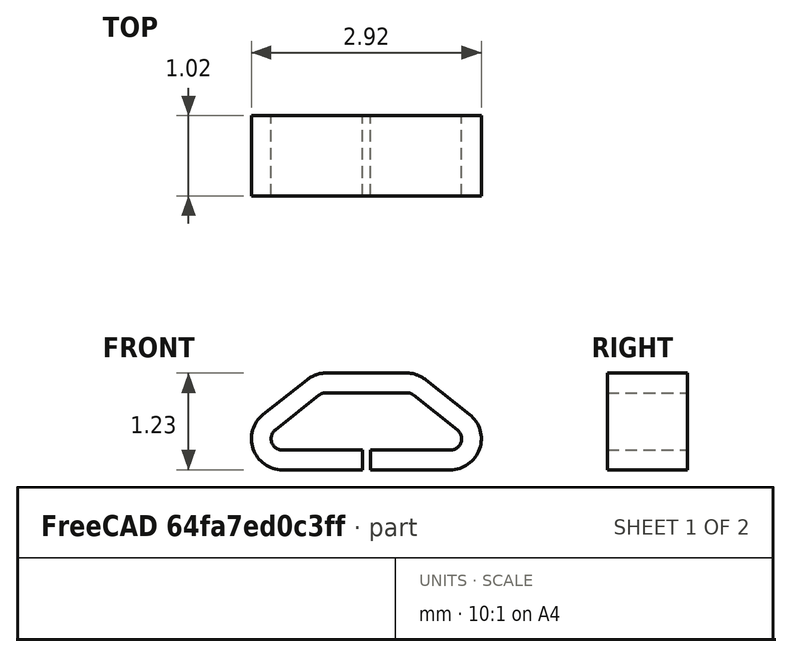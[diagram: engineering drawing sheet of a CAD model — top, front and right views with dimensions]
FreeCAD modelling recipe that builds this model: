
FCSTD DOCUMENT  (FreeCAD 1.0R39109 (Git))
Label: RH-5015
License: All rights reserved
LicenseURL: http://en.wikipedia.org/wiki/All_rights_reserved
objects: Sketcher::SketchObject×2, PartDesign::AdditivePipe×1, PartDesign::Body×1
note: 8 computed .brp shape members not serialized (recipe doc carries the construction recipe); baked Part::Feature solids carry a one-line shape summary decoded from their .brp

FEATURE [Sketcher::SketchObject] Sketch  label="RH-5015 trj"
  ArcFitTolerance = 1e-06
  AttachmentSupport = -> [XZ_Plane]
  FullyConstrained = true
  MakeInternals = false
  MapMode = 5
  Placement = pos=(0,0,0) rot=(1,0,0;1.5708rad)
  sketch-geometry (13):
    g0: LineSegment StartX=0.05 StartY=0.125 StartZ=0 EndX=1.065 EndY=0.125 EndZ=0
    g1: LineSegment StartX=1.23274 StartY=0.606576 StartZ=0 EndX=0.677736 EndY=1.04658 EndZ=0
    g2: LineSegment StartX=0.51 StartY=1.105 StartZ=0 EndX=-0.51 EndY=1.105 EndZ=0
    g3: LineSegment StartX=-0.677736 StartY=1.04658 StartZ=0 EndX=-1.23274 EndY=0.606576 EndZ=0
    g4: LineSegment StartX=-1.065 StartY=0.125 StartZ=0 EndX=-0.05 EndY=0.125 EndZ=0
    g5: ArcOfCircle CenterX=1.065 CenterY=0.395 CenterZ=0 NormalX=0 NormalY=0 NormalZ=1 AngleXU=0 Radius=0.27 StartAngle=4.71239 EndAngle=7.18365
    g6: GeomPoint [constr] X=1.84018 Y=0.125 Z=0
    g7: ArcOfCircle CenterX=0.51 CenterY=0.835 CenterZ=0 NormalX=0 NormalY=0 NormalZ=1 AngleXU=0 Radius=0.27 StartAngle=0.900465 EndAngle=1.5708
    g8: GeomPoint [constr] X=0.604043 Y=1.105 Z=0
    g9: ArcOfCircle CenterX=-0.51 CenterY=0.835 CenterZ=0 NormalX=0 NormalY=0 NormalZ=1 AngleXU=0 Radius=0.27 StartAngle=1.5708 EndAngle=2.24113
    g10: GeomPoint [constr] X=-0.604043 Y=1.105 Z=0
    g11: ArcOfCircle CenterX=-1.065 CenterY=0.395 CenterZ=0 NormalX=0 NormalY=0 NormalZ=1 AngleXU=0 Radius=0.27 StartAngle=2.24113 EndAngle=4.71239
    g12: GeomPoint [constr] X=-1.84018 Y=0.125 Z=0
  constraints (29):
    c: Horizontal(g0)
    c: Horizontal(g2)
    c: Horizontal(g4)
    c: PointOnObject(g6,g0)
    c: PointOnObject(g6,g1)
    c: Tangent(g0,g5) = -1.5708
    c: Tangent(g1,g5) = -1.5708
    c: PointOnObject(g8,g1)
    c: PointOnObject(g8,g2)
    c: Tangent(g1,g7) = -1.5708
    c: Tangent(g2,g7) = -1.5708
    c: PointOnObject(g10,g2)
    c: PointOnObject(g10,g3)
    c: Tangent(g2,g9) = -1.5708
    c: Tangent(g3,g9) = -1.5708
    c: PointOnObject(g12,g4)
    c: PointOnObject(g12,g3)
    c: Tangent(g4,g11) = -1.5708
    c: Tangent(g3,g11) = -1.5708
    c: Symmetric(g11,g5,g-2)
    c: Symmetric(g7,g9,g-2)
    c: Equal(g5,g7)
    c: DistanceX(g9,g7) = 1.02
    c: Symmetric(g0,g4,g-2)
    c: DistanceX(g4,g0) = 0.1
    c: DistanceY(g-1,g0) = 0.125
    c: Radius(g5) = 0.27
    c: DistanceX(g11,g5) = 2.13
    c: DistanceY(g0,g2) = 0.98
FEATURE [Sketcher::SketchObject] Sketch001  label="RH-5015 crs"
  ArcFitTolerance = 1e-06
  AttachmentSupport = -> [YZ_Plane]
  ExternalGeometry = -> [Sketch]
  FullyConstrained = true
  MakeInternals = false
  MapMode = 5
  Placement = pos=(0,0,0) rot=(0.57735,0.57735,0.57735;2.0944rad)
  sketch-geometry (4):
    g0: LineSegment StartX=-0.51 StartY=1.23 StartZ=0 EndX=-0.51 EndY=0.98 EndZ=0
    g1: LineSegment StartX=-0.51 StartY=0.98 StartZ=0 EndX=0.51 EndY=0.98 EndZ=0
    g2: LineSegment StartX=0.51 StartY=0.98 StartZ=0 EndX=0.51 EndY=1.23 EndZ=0
    g3: LineSegment StartX=0.51 StartY=1.23 StartZ=0 EndX=-0.51 EndY=1.23 EndZ=0
  constraints (11):
    c: Coincident(g0,g1)
    c: Coincident(g1,g2)
    c: Coincident(g2,g3)
    c: Coincident(g3,g0)
    c: Vertical(g0)
    c: Vertical(g2)
    c: Horizontal(g1)
    c: Horizontal(g3)
    c: DistanceY(g2,g2) = 0.25
    c: DistanceX(g3,g3) = 1.02
    c: Symmetric(g0,g2,g-3)
FEATURE [PartDesign::AdditivePipe] AdditivePipe  label="RH-5016"
  AuxilleryCurvelinear = true
  AuxillerySpineTangent = false
  Binormal = (0,0,0)
  Mode = 0
  Placement = pos=(0,0,0) rot=(1,1,1;2.0944rad)
  Profile = -> Sketch001
  Refine = true
  Spine = -> Sketch
  SpineTangent = false
  Suppressed = false
  Transformation = 0
  Transition = 0
FEATURE [PartDesign::Body] Body  label="RH-5015"
  AllowCompound = false
  Group = -> [Sketch,Sketch001,AdditivePipe]
  Origin = -> Origin
  Tip = -> AdditivePipe
